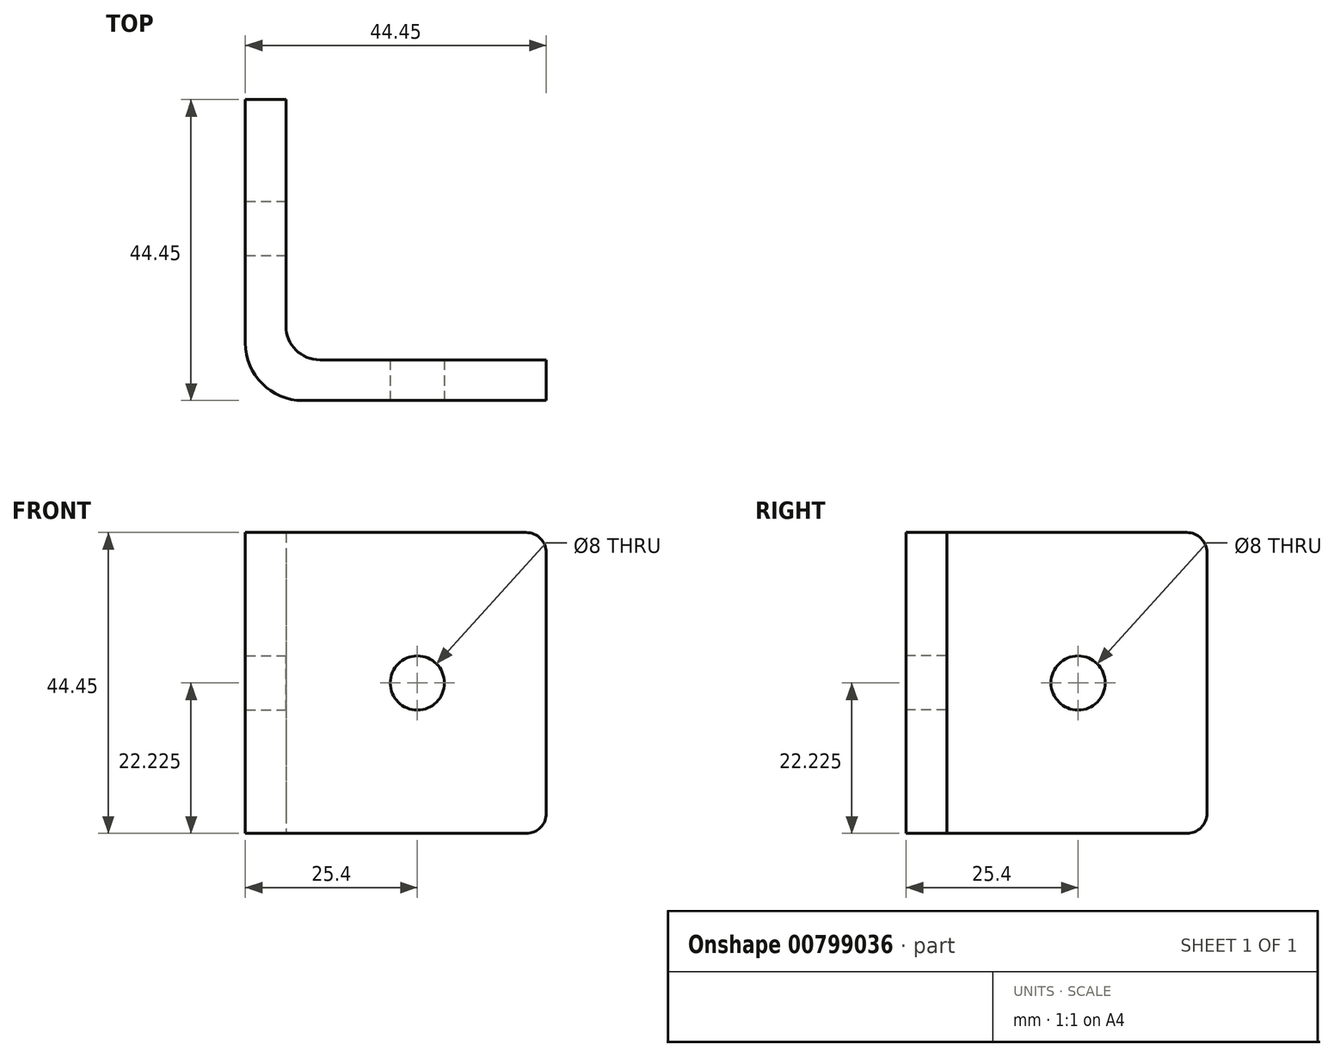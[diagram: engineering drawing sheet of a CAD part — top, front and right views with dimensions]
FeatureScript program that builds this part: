
annotation { "Feature Type Name" : "Feature", "Feature Type Description" : "" }
export const myFeature = defineFeature(function(context is Context, id is Id, definition is map)
    precondition{}
    {
        {
            var Q0;
            Q0=qCreatedBy(makeId("Top.planeOp"),FACE);
            var sketch = newSketch(context, id + "F0", { "sketchPlane" : qUnion([Q0])});
            skLineSegment(sketch, "E0", {"start": v(0, 44.45) * mm, "end": v(0, 8.5) * mm});
            skLineSegment(sketch, "E1", {"start": v(8.5, 0) * mm, "end": v(44.45, 0) * mm});
            skLineSegment(sketch, "E2", {"start": v(44.45, 0) * mm, "end": v(44.45, 6) * mm});
            skLineSegment(sketch, "E3", {"start": v(44.45, 6) * mm, "end": v(11, 6) * mm});
            skLineSegment(sketch, "E4", {"start": v(6, 11) * mm, "end": v(6, 44.45) * mm});
            skLineSegment(sketch, "E5", {"start": v(6, 44.45) * mm, "end": v(0, 44.45) * mm});
            skPoint(sketch, "E6.visualSharp", {"position": v(0, 0) * mm});
            skArc(sketch, "E6.filletArc", {"start": v(0, 8.5) * mm, "mid": v(2.49, 2.49) * mm, "end": v(8.5, 0) * mm});
            skPoint(sketch, "E7.visualSharp", {"position": v(6, 6) * mm});
            skArc(sketch, "E7.filletArc", {"start": v(6, 11) * mm, "mid": v(7.46, 7.46) * mm, "end": v(11, 6) * mm});
            skSolve(sketch);
        }
        {
            var Q0;
            Q0=qSketchRegion(id+"F0",true);
            extrude(context, id + "F1", {"entities" : qUnion([Q0]), "depth" : 44.45 * mm, "offsetDistance" : 25 * mm});
        }
        {
            var Q0;
            Q0=makeQuery(id+"F1.opExtrude","SWEPT_FACE",FACE,{"disambiguationData":[OSD([sQuery(id+"F0.wireOp",EDGE,"E4")])]});
            var sketch = newSketch(context, id + "F2", { "sketchPlane" : qUnion([Q0])});
            skLineSegment(sketch, "E8", {"start": v(44.45, 22.23) * mm, "end": v(0, 22.23) * mm, "construction": true});
            skCircle(sketch, "E9", {"center": v(25.4, 22.22) * mm, "radius": 4 * mm});
            skSolve(sketch);
        }
        {
            var Q0;
            Q0=qSketchRegion(id+"F2",true);
            extrude(context, id + "F3", {"entities" : qUnion([Q0]), "operationType" : NewBodyOperationType.REMOVE, "endBound" : BoundingType.UP_TO_NEXT, "oppositeDirection" : true, "depth" : 25 * mm, "offsetDistance" : 25 * mm});
        }
        {
            var Q0;
            Q0=makeQuery(id+"F1.opExtrude","SWEPT_FACE",FACE,{"disambiguationData":[OSD([sQuery(id+"F0.wireOp",EDGE,"E1")])]});
            var sketch = newSketch(context, id + "F4", { "sketchPlane" : qUnion([Q0])});
            skLineSegment(sketch, "E10", {"start": v(44.45, 22.23) * mm, "end": v(0, 22.23) * mm, "construction": true});
            skCircle(sketch, "E11", {"center": v(25.4, 22.22) * mm, "radius": 4 * mm});
            skSolve(sketch);
        }
        {
            var Q0;
            Q0=qSketchRegion(id+"F4",true);
            extrude(context, id + "F5", {"entities" : qUnion([Q0]), "operationType" : NewBodyOperationType.REMOVE, "endBound" : BoundingType.UP_TO_NEXT, "oppositeDirection" : true, "depth" : 25 * mm, "offsetDistance" : 25 * mm});
        }
        {
            var Q0;
            Q0=makeQuery(id+"F1.opExtrude","CAP_EDGE",EDGE,{"disambiguationData":[OSD([sQuery(id+"F0.wireOp",EDGE,"E2")])],"isStart":false});
            var Q1;
            Q1=makeQuery(id+"F1.opExtrude","CAP_EDGE",EDGE,{"disambiguationData":[OSD([sQuery(id+"F0.wireOp",EDGE,"E2")])],"isStart":true});
            var Q2;
            Q2=makeQuery(id+"F1.opExtrude","CAP_EDGE",EDGE,{"disambiguationData":[OSD([sQuery(id+"F0.wireOp",EDGE,"E5")])],"isStart":true});
            var Q3;
            Q3=makeQuery(id+"F1.opExtrude","CAP_EDGE",EDGE,{"disambiguationData":[OSD([sQuery(id+"F0.wireOp",EDGE,"E5")])],"isStart":false});
            fillet(context, id + "F6", {"entities" : qUnion([Q0, Q1, Q2, Q3]), "radius" : 3 * mm, "tangentPropagation" : true, "allowEdgeOverflow" : false});
        }
    });
